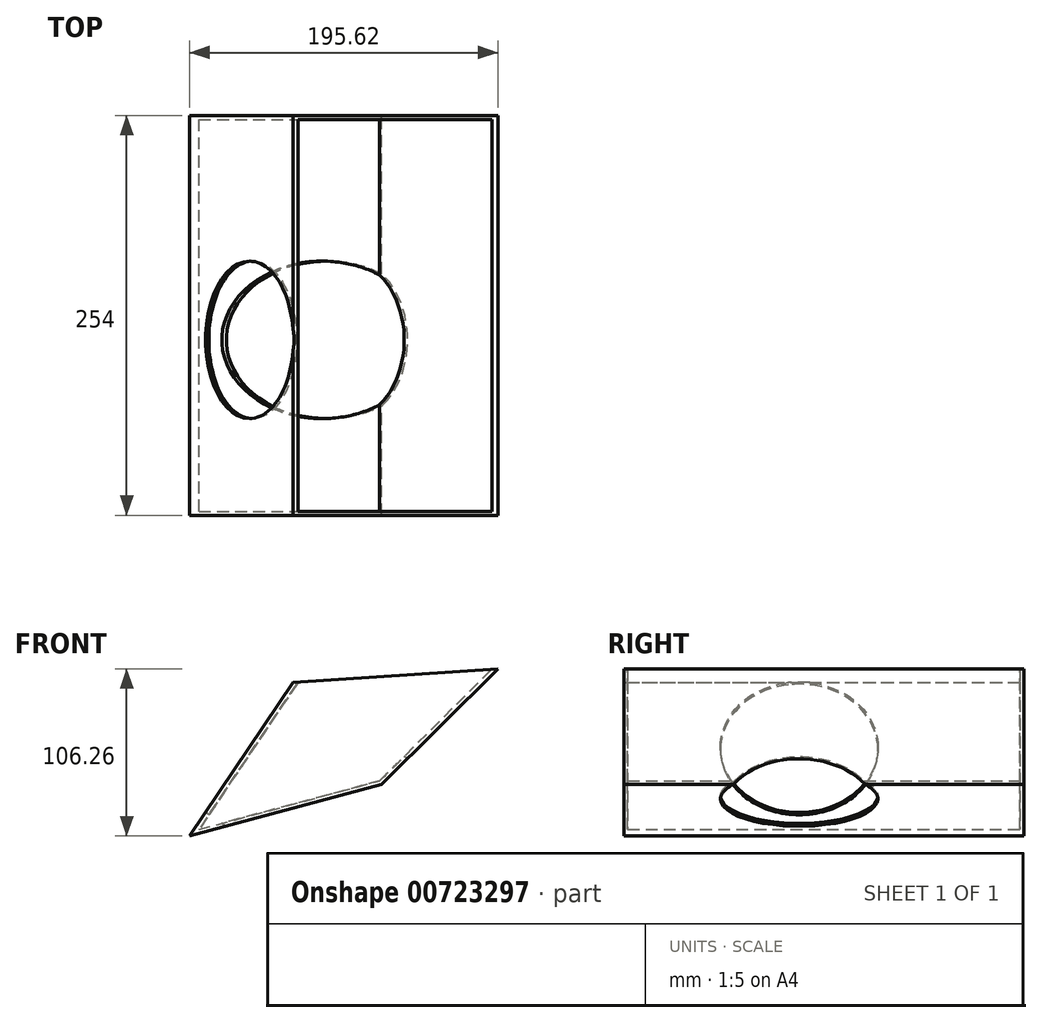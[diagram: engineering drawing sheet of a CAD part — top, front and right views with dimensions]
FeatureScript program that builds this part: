
annotation { "Feature Type Name" : "Feature", "Feature Type Description" : "" }
export const myFeature = defineFeature(function(context is Context, id is Id, definition is map)
    precondition{}
    {
        {
            var Q0;
            Q0=qCreatedBy(makeId("Front.planeOp"),FACE);
            var sketch = newSketch(context, id + "F0", { "sketchPlane" : qUnion([Q0])});
            skLineSegment(sketch, "E0", {"start": v(111.35, 39.49) * mm, "end": v(185.05, 112.94) * mm});
            skLineSegment(sketch, "E1", {"start": v(185.05, 112.94) * mm, "end": v(55, 104.22) * mm});
            skLineSegment(sketch, "E2", {"start": v(55, 104.22) * mm, "end": v(-10.57, 6.68) * mm});
            skLineSegment(sketch, "E3", {"start": v(-10.57, 6.68) * mm, "end": v(111.35, 39.49) * mm});
            skSolve(sketch);
        }
        {
            var Q0;
            Q0=makeQuery(id+"F0.imprint","IMPRINT",FACE,{"disambiguationData":[TD([[makeQuery(id+"F0.imprint","IMPRINT",EDGE,{"derivedFrom":sQuery(id+"F0.wireOp",EDGE,"E0")}),1.0]])]});
            extrude(context, id + "F1", {"entities" : qUnion([Q0]), "depth" : 254 * mm, "offsetDistance" : 25.4 * mm});
        }
        {
            var Q0;
            Q0=makeQuery(id+"F1.opExtrude","SWEPT_FACE",FACE,{"disambiguationData":[OSD([sQuery(id+"F0.wireOp",EDGE,"E1")])]});
            shell(context, id + "F2", {"entities" : qUnion([Q0]), "thickness" : 2.5 * mm});
        }
        {
            var Q0;
            Q0=makeQuery(id+"F1.opExtrude","SWEPT_FACE",FACE,{"disambiguationData":[OSD([sQuery(id+"F0.wireOp",EDGE,"E2")])]});
            var sketch = newSketch(context, id + "F3", { "sketchPlane" : qUnion([Q0])});
            skCircle(sketch, "E4", {"center": v(142.57, 67.63) * mm, "radius": 22.2 * mm});
            skSolve(sketch);
        }
        {
            var Q0;
            Q0=sQuery(id+"F3.wireOp",VERTEX,"E4.center");
            var Q1;
            Q1=makeQuery(id+"F1.opExtrude","SWEPT_BODY",BODY,{"disambiguationData":[OSD([sQuery(id+"F0.wireOp",EDGE,"E0"),sQuery(id+"F0.wireOp",EDGE,"E1"),sQuery(id+"F0.wireOp",EDGE,"E2"),sQuery(id+"F0.wireOp",EDGE,"E3")])]});
            hole(context, id + "F4", {"style" : HoleStyle.SIMPLE, "endStyle" : HoleEndStyle.THROUGH, "holeDiameter" : 100 * mm, "majorDiameter" : 5 * mm, "isTappedThrough" : true, "tappedDepth" : 12 * mm, "tapClearance" : 3, "locations" : qUnion([Q0]), "scope" : qUnion([Q1])});
        }
    });
